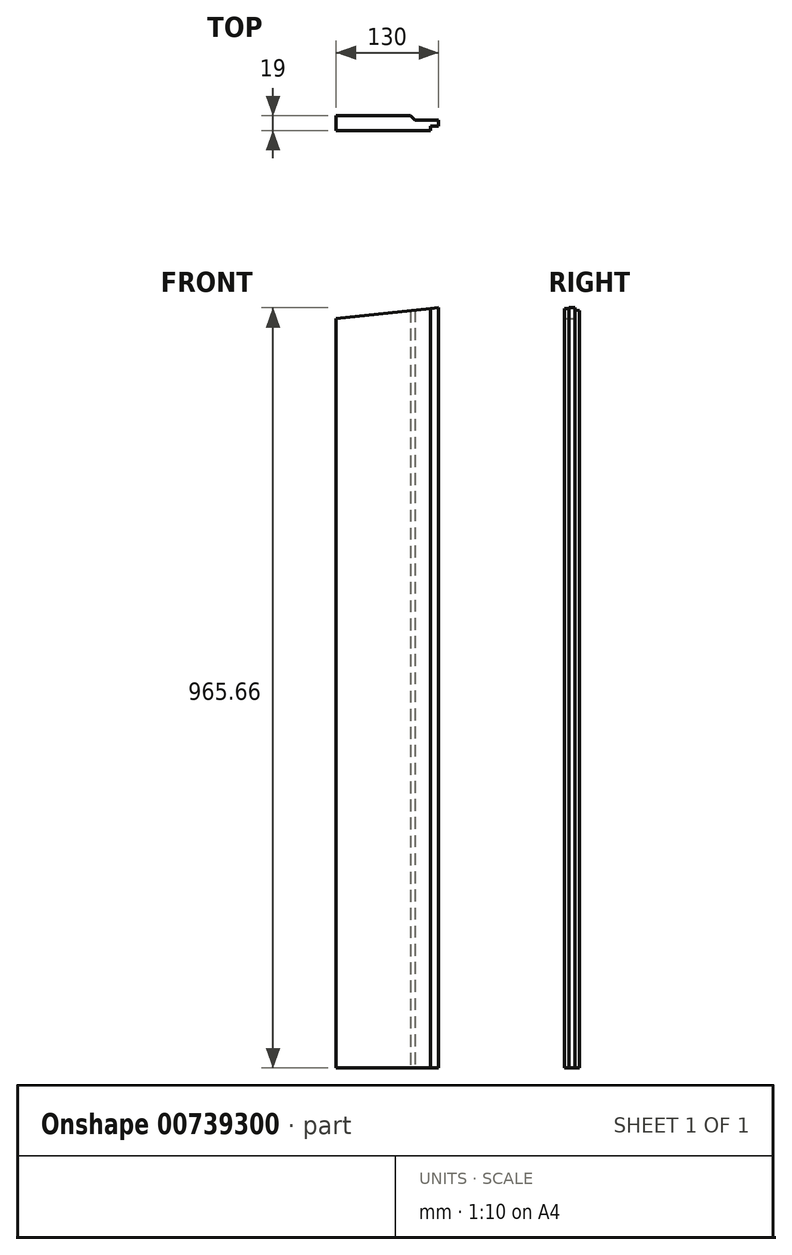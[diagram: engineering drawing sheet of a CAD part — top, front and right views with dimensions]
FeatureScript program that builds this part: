
annotation { "Feature Type Name" : "Feature", "Feature Type Description" : "" }
export const myFeature = defineFeature(function(context is Context, id is Id, definition is map)
    precondition{}
    {
        {
            var Q0;
            Q0=qCreatedBy(makeId("Top.planeOp"),FACE);
            var sketch = newSketch(context, id + "F0", { "sketchPlane" : qUnion([Q0])});
            skLineSegment(sketch, "E0.bottom", {"start": v(0, -9.5) * mm, "end": v(136, -9.5) * mm});
            skLineSegment(sketch, "E0.top", {"start": v(0, 9.5) * mm, "end": v(110.5, 9.5) * mm});
            skLineSegment(sketch, "E0.left", {"start": v(0, -9.5) * mm, "end": v(0, -4) * mm});
            skLineSegment(sketch, "E0.right", {"start": v(136, -9.5) * mm, "end": v(136, -4) * mm});
            skLineSegment(sketch, "E1", {"start": v(0, -4) * mm, "end": v(12, -4) * mm});
            skLineSegment(sketch, "E2", {"start": v(12, -4) * mm, "end": v(12, 4) * mm});
            skLineSegment(sketch, "E3", {"start": v(12, 4) * mm, "end": v(0, 4) * mm});
            skLineSegment(sketch, "E4.trimOffspring", {"start": v(0, 4) * mm, "end": v(0, 9.5) * mm});
            skLineSegment(sketch, "E5", {"start": v(136, -4) * mm, "end": v(146, -4) * mm});
            skLineSegment(sketch, "E6", {"start": v(146, -4) * mm, "end": v(146, 4) * mm});
            skLineSegment(sketch, "E7", {"start": v(146, 4) * mm, "end": v(116, 4) * mm});
            skLineSegment(sketch, "E8.trimOffspring", {"start": v(116, 4) * mm, "end": v(110.5, 9.5) * mm});
            skSolve(sketch);
        }
        {
            var Q0;
            Q0=makeQuery(id+"F0.imprint","IMPRINT",FACE,{"disambiguationData":[TD([[makeQuery(id+"F0.imprint","IMPRINT",EDGE,{"derivedFrom":sQuery(id+"F0.wireOp",EDGE,"E0.bottom")}),1.0]])]});
            extrude(context, id + "F1", {"entities" : qUnion([Q0]), "depth" : 1100 * mm, "offsetDistance" : 25 * mm});
        }
        {
            var Q0;
            Q0=makeQuery(id+"F1.opExtrude","CAP_FACE",FACE,{"disambiguationData":[OSD([sQuery(id+"F0.wireOp",EDGE,"E0.bottom"),sQuery(id+"F0.wireOp",EDGE,"E0.top"),sQuery(id+"F0.wireOp",EDGE,"E0.left"),sQuery(id+"F0.wireOp",EDGE,"E0.right"),sQuery(id+"F0.wireOp",EDGE,"E1"),sQuery(id+"F0.wireOp",EDGE,"E2"),sQuery(id+"F0.wireOp",EDGE,"E3"),sQuery(id+"F0.wireOp",EDGE,"E4.trimOffspring"),sQuery(id+"F0.wireOp",EDGE,"E5"),sQuery(id+"F0.wireOp",EDGE,"E6"),sQuery(id+"F0.wireOp",EDGE,"E7"),sQuery(id+"F0.wireOp",EDGE,"E8.trimOffspring")])],"isStart":true});
            var sketch = newSketch(context, id + "F2", { "sketchPlane" : qUnion([Q0])});
            skLineSegment(sketch, "E9", {"start": v(16, -9.5) * mm, "end": v(16, 9.5) * mm});
            skSolve(sketch);
        }
        {
            var Q0;
            {var subQ1=sQuery(id+"F2.wireOp",EDGE,"E9");Q0=makeQuery(id+"F2.imprint","IMPRINT",FACE,{"disambiguationData":[TD([[makeQuery(id+"F2.imprint","IMPRINT",EDGE,{"derivedFrom":subQ1}),1.0]])]});}
            extrude(context, id + "F3", {"entities" : qUnion([Q0]), "operationType" : NewBodyOperationType.REMOVE, "endBound" : BoundingType.THROUGH_ALL, "oppositeDirection" : true, "depth" : 25 * mm, "offsetDistance" : 25 * mm});
        }
        {
            var Q0;
            Q0=makeQuery(id+"F1.opExtrude","SWEPT_FACE",FACE,{"disambiguationData":[OSD([sQuery(id+"F0.wireOp",EDGE,"E0.top")])]});
            var sketch = newSketch(context, id + "F4", { "sketchPlane" : qUnion([Q0])});
            skLineSegment(sketch, "E10", {"start": v(-1424.15, 1100) * mm, "end": v(3, 950) * mm});
            skLineSegment(sketch, "E11", {"start": v(3, 950) * mm, "end": v(3, 1100) * mm});
            skLineSegment(sketch, "E12", {"start": v(3, 1100) * mm, "end": v(-1424.15, 1100) * mm});
            skSolve(sketch);
        }
        {
            var Q0;
            {var subQ0=sQuery(id+"F4.wireOp",EDGE,"E12");var subQ1=sQuery(id+"F4.wireOp",EDGE,"E10");var subQ2=makeQuery(id+"F4.imprint","INTERSECT",VERTEX,{"derivedFrom":[subQ1,subQ0]});Q0=makeQuery(id+"F4.imprint","IMPRINT",FACE,{"disambiguationData":[TD([[makeQuery(id+"F4.imprint","IMPRINT",EDGE,{"disambiguationData":[TD([[subQ2,-1.0]])],"derivedFrom":subQ1}),1.0]])]});}
            var Q1;
            {var subQ0=sQuery(id+"F4.wireOp",EDGE,"E11");Q1=makeQuery(id+"F4.imprint","IMPRINT",FACE,{"disambiguationData":[TD([[makeQuery(id+"F4.imprint","IMPRINT",EDGE,{"derivedFrom":subQ0}),1.0]])]});}
            var Q2;
            {var subQ0=sQuery(id+"F4.wireOp",EDGE,"E10");var subQ1=sQuery(id+"F0.wireOp",EDGE,"E0.top");var subQ2=makeQuery(id+"F1.opExtrude","SWEPT_EDGE",EDGE,{"disambiguationData":[OSD([subQ1,sQuery(id+"F0.wireOp",EDGE,"E8.trimOffspring")])]});var subQ3=makeQuery(id+"F4.imprint","INTERSECT",VERTEX,{"derivedFrom":[subQ2,subQ0]});Q2=makeQuery(id+"F4.imprint","IMPRINT",FACE,{"disambiguationData":[TD([[makeQuery(id+"F4.imprint","IMPRINT",EDGE,{"disambiguationData":[TD([[subQ3,-1.0]])],"derivedFrom":subQ0}),1.0]])]});}
            extrude(context, id + "F5", {"entities" : qUnion([Q0, Q1, Q2]), "operationType" : NewBodyOperationType.REMOVE, "endBound" : BoundingType.THROUGH_ALL, "oppositeDirection" : true, "depth" : 25 * mm, "offsetDistance" : 25 * mm});
        }
    });
